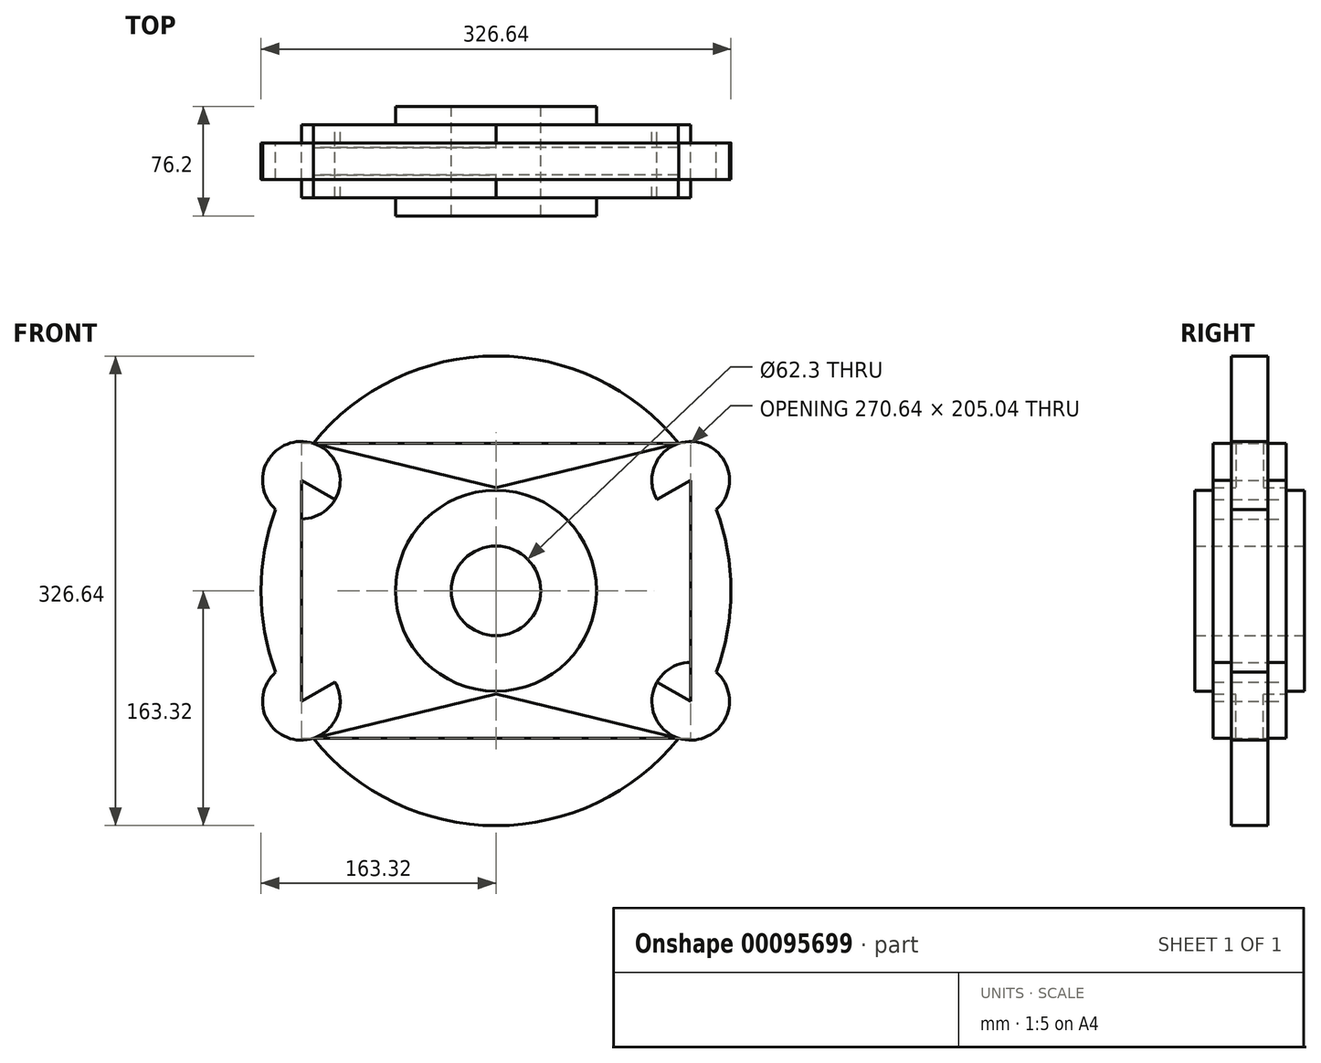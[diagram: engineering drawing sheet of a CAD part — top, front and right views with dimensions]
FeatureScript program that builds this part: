
annotation { "Feature Type Name" : "Feature", "Feature Type Description" : "" }
export const myFeature = defineFeature(function(context is Context, id is Id, definition is map)
    precondition{}
    {
        {
            var Q0;
            Q0=qCreatedBy(makeId("Front.planeOp"),FACE);
            var sketch = newSketch(context, id + "F0", { "sketchPlane" : qUnion([Q0])});
            skCircle(sketch, "E0", {"center": v(0, 0) * mm, "radius": 69.85 * mm});
            skCircle(sketch, "E1", {"center": v(135.32, 76.89) * mm, "radius": 26.99 * mm});
            skLineSegment(sketch, "E2", {"start": v(126.88, 102.52) * mm, "end": v(0, 71.86) * mm});
            skCircle(sketch, "E3.MirrorC", {"center": v(135.32, -76.89) * mm, "radius": 26.99 * mm});
            skLineSegment(sketch, "E4.MirrorCS", {"start": v(126.88, -102.52) * mm, "end": v(0, -71.86) * mm});
            skLineSegment(sketch, "E5.MirrorCS", {"start": v(-126.88, 102.52) * mm, "end": v(0, 71.86) * mm});
            skCircle(sketch, "E6.MirrorC", {"center": v(-135.32, 76.89) * mm, "radius": 26.99 * mm});
            skCircle(sketch, "E7.MirrorC", {"center": v(-135.32, -76.89) * mm, "radius": 26.99 * mm});
            skLineSegment(sketch, "E8.MirrorCS", {"start": v(-126.88, -102.52) * mm, "end": v(0, -71.86) * mm});
            skCircle(sketch, "E9.0", {"center": v(0, 0) * mm, "radius": 163.32 * mm});
            skLineSegment(sketch, "E10", {"start": v(135.32, 76.89) * mm, "end": v(0, 0) * mm});
            skLineSegment(sketch, "E11", {"start": v(135.32, -76.89) * mm, "end": v(0, 0) * mm});
            skLineSegment(sketch, "E12", {"start": v(-135.32, -76.89) * mm, "end": v(0, 0) * mm});
            skLineSegment(sketch, "E13", {"start": v(-135.32, 76.89) * mm, "end": v(0, 0) * mm});
            skLineSegment(sketch, "E14", {"start": v(-135.32, 76.89) * mm, "end": v(-135.32, -76.89) * mm});
            skLineSegment(sketch, "E15", {"start": v(135.32, 76.89) * mm, "end": v(135.32, -76.89) * mm});
            skLineSegment(sketch, "E16", {"start": v(-126.88, 102.52) * mm, "end": v(126.88, 102.52) * mm});
            skLineSegment(sketch, "E17", {"start": v(126.88, -102.52) * mm, "end": v(-126.88, -102.52) * mm});
            skCircle(sketch, "E18", {"center": v(0, 0) * mm, "radius": 31.15 * mm});
            skSolve(sketch);
        }
        {
            var Q0;
            Q0 = qSketchRegion(id + "F0", true);
            var Q1;
            {var subQ0=sQuery(id+"F0.wireOp",EDGE,"E2");Q1=makeQuery(id+"F0.imprint","IMPRINT",FACE,{"disambiguationData":[TD([[makeQuery(id+"F0.imprint","IMPRINT",EDGE,{"derivedFrom":subQ0}),1.0]])]});}
            var Q2;
            {var subQ0=sQuery(id+"F0.wireOp",EDGE,"E4.MirrorCS");Q2=makeQuery(id+"F0.imprint","IMPRINT",FACE,{"disambiguationData":[TD([[makeQuery(id+"F0.imprint","IMPRINT",EDGE,{"derivedFrom":subQ0}),-1.0]])]});}
            extrude(context, id + "F1", {"entities" : qUnion([Q0, Q1, Q2]), "endBound" : BoundingType.SYMMETRIC, "depth" : 25.4 * mm});
        }
        {
            var Q0;
            {var subQ0=sQuery(id+"F0.wireOp",EDGE,"E13");var subQ1=sQuery(id+"F0.wireOp",EDGE,"E6.MirrorC");var subQ2=makeQuery(id+"F0.imprint","INTERSECT",VERTEX,{"derivedFrom":[subQ1,subQ0]});Q0=makeQuery(id+"F0.imprint","IMPRINT",FACE,{"disambiguationData":[TD([[makeQuery(id+"F0.imprint","IMPRINT",EDGE,{"disambiguationData":[TD([[subQ2,-1.0]])],"derivedFrom":subQ1}),-1.0]])]});}
            var Q1;
            {var subQ0=sQuery(id+"F0.wireOp",EDGE,"E12");var subQ1=sQuery(id+"F0.wireOp",EDGE,"E7.MirrorC");var subQ2=makeQuery(id+"F0.imprint","INTERSECT",VERTEX,{"derivedFrom":[subQ1,subQ0]});Q1=makeQuery(id+"F0.imprint","IMPRINT",FACE,{"disambiguationData":[TD([[makeQuery(id+"F0.imprint","IMPRINT",EDGE,{"disambiguationData":[TD([[subQ2,-1.0]])],"derivedFrom":subQ1}),1.0]])]});}
            var Q2;
            {var subQ0=sQuery(id+"F0.wireOp",EDGE,"E11");var subQ1=sQuery(id+"F0.wireOp",EDGE,"E3.MirrorC");var subQ2=makeQuery(id+"F0.imprint","INTERSECT",VERTEX,{"derivedFrom":[subQ1,subQ0]});Q2=makeQuery(id+"F0.imprint","IMPRINT",FACE,{"disambiguationData":[TD([[makeQuery(id+"F0.imprint","IMPRINT",EDGE,{"disambiguationData":[TD([[subQ2,-1.0]])],"derivedFrom":subQ1}),-1.0]])]});}
            var Q3;
            {var subQ0=sQuery(id+"F0.wireOp",EDGE,"E10");var subQ1=sQuery(id+"F0.wireOp",EDGE,"E1");var subQ2=makeQuery(id+"F0.imprint","INTERSECT",VERTEX,{"derivedFrom":[subQ1,subQ0]});Q3=makeQuery(id+"F0.imprint","IMPRINT",FACE,{"disambiguationData":[TD([[makeQuery(id+"F0.imprint","IMPRINT",EDGE,{"disambiguationData":[TD([[subQ2,-1.0]])],"derivedFrom":subQ1}),1.0]])]});}
            var Q4;
            {var subQ1=sQuery(id+"F0.wireOp",EDGE,"E0");var subQ7=sQuery(id+"F0.wireOp",EDGE,"E13");var subQ11=makeQuery(id+"F0.imprint","INTERSECT",VERTEX,{"derivedFrom":[subQ1,subQ7]});Q4=makeQuery(id+"F0.imprint","IMPRINT",FACE,{"disambiguationData":[TD([[makeQuery(id+"F0.imprint","IMPRINT",EDGE,{"disambiguationData":[TD([[subQ11,-1.0]])],"derivedFrom":subQ1}),-1.0]])]});}
            var Q5;
            {var subQ5=sQuery(id+"F0.wireOp",EDGE,"E10");var subQ6=sQuery(id+"F0.wireOp",EDGE,"E0");var subQ7=makeQuery(id+"F0.imprint","INTERSECT",VERTEX,{"derivedFrom":[subQ6,subQ5]});Q5=makeQuery(id+"F0.imprint","IMPRINT",FACE,{"disambiguationData":[TD([[makeQuery(id+"F0.imprint","IMPRINT",EDGE,{"disambiguationData":[TD([[subQ7,1.0]])],"derivedFrom":subQ6}),-1.0]])]});}
            extrude(context, id + "F2", {"entities" : qUnion([Q0, Q1, Q2, Q3, Q4, Q5]), "operationType" : NewBodyOperationType.ADD, "endBound" : BoundingType.SYMMETRIC, "depth" : 50.8 * mm});
        }
        {
            var Q0;
            {var subQ0=sQuery(id+"F0.wireOp",EDGE,"E12");var subQ1=sQuery(id+"F0.wireOp",EDGE,"E0");var subQ2=makeQuery(id+"F0.imprint","INTERSECT",VERTEX,{"derivedFrom":[subQ1,subQ0]});Q0=makeQuery(id+"F0.imprint","IMPRINT",FACE,{"disambiguationData":[TD([[makeQuery(id+"F0.imprint","IMPRINT",EDGE,{"disambiguationData":[TD([[subQ2,-1.0]])],"derivedFrom":subQ1}),1.0]])]});}
            var Q1;
            {var subQ0=sQuery(id+"F0.wireOp",EDGE,"E13");var subQ1=sQuery(id+"F0.wireOp",EDGE,"E0");var subQ2=makeQuery(id+"F0.imprint","INTERSECT",VERTEX,{"derivedFrom":[subQ1,subQ0]});Q1=makeQuery(id+"F0.imprint","IMPRINT",FACE,{"disambiguationData":[TD([[makeQuery(id+"F0.imprint","IMPRINT",EDGE,{"disambiguationData":[TD([[subQ2,1.0]])],"derivedFrom":subQ1}),1.0]])]});}
            var Q2;
            {var subQ0=sQuery(id+"F0.wireOp",EDGE,"E10");var subQ1=sQuery(id+"F0.wireOp",EDGE,"E0");var subQ2=makeQuery(id+"F0.imprint","INTERSECT",VERTEX,{"derivedFrom":[subQ1,subQ0]});Q2=makeQuery(id+"F0.imprint","IMPRINT",FACE,{"disambiguationData":[TD([[makeQuery(id+"F0.imprint","IMPRINT",EDGE,{"disambiguationData":[TD([[subQ2,1.0]])],"derivedFrom":subQ1}),1.0]])]});}
            var Q3;
            {var subQ0=sQuery(id+"F0.wireOp",EDGE,"E13");var subQ1=sQuery(id+"F0.wireOp",EDGE,"E0");var subQ2=makeQuery(id+"F0.imprint","INTERSECT",VERTEX,{"derivedFrom":[subQ1,subQ0]});Q3=makeQuery(id+"F0.imprint","IMPRINT",FACE,{"disambiguationData":[TD([[makeQuery(id+"F0.imprint","IMPRINT",EDGE,{"disambiguationData":[TD([[subQ2,-1.0]])],"derivedFrom":subQ1}),1.0]])]});}
            extrude(context, id + "F3", {"entities" : qUnion([Q0, Q1, Q2, Q3]), "operationType" : NewBodyOperationType.ADD, "endBound" : BoundingType.SYMMETRIC, "depth" : 76.2 * mm});
        }
        {
            var Q0;
            Q0=makeQuery(id+"F0.imprint","IMPRINT",FACE,{"disambiguationData":[TD([[makeQuery(id+"F0.imprint","IMPRINT",EDGE,{"derivedFrom":sQuery(id+"F0.wireOp",EDGE,"E2")}),-1.0]])]});
            var Q1;
            Q1=makeQuery(id+"F0.imprint","IMPRINT",FACE,{"disambiguationData":[TD([[makeQuery(id+"F0.imprint","IMPRINT",EDGE,{"derivedFrom":sQuery(id+"F0.wireOp",EDGE,"E4.MirrorCS")}),1.0]])]});
            extrude(context, id + "F4", {"entities" : qUnion([Q0, Q1]), "operationType" : NewBodyOperationType.ADD, "endBound" : BoundingType.SYMMETRIC, "depth" : 19.05 * mm});
        }
    });
